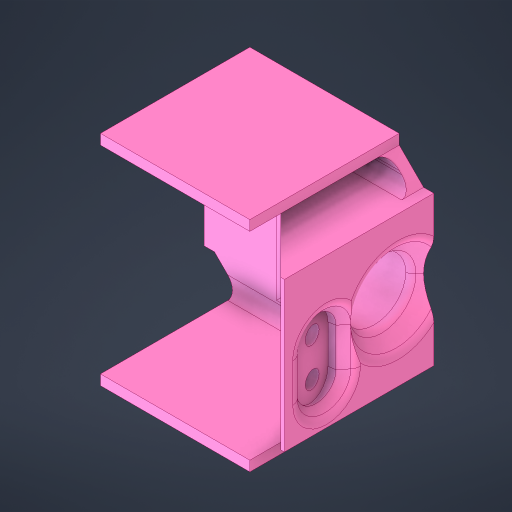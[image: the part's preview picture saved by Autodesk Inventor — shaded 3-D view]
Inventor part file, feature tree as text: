
AUTODESK INVENTOR PART (.ipt)
format: ipt  version: 2023.4 (Build 274418000, 418)  size: 642,560 bytes
history: native  units: mm
features: projected_geometry x15, extrude x14, chamfer x2, other x2, plane x1, fillet x1, reference x1
ambient origin geometry x8: Origin, YZ Plane, XZ Plane, XY Plane, X Axis, Y Axis, Z Axis, Center Point
bodies: Solid1 (feature_tree)
feature tree (36):
  plane  "Work Plane1"
  extrude  "Extrusion1"  Depth=2.5mm TaperAngle=0.0deg
  extrude  "Extrusion2"  Depth=0.075mm
  extrude  "Extrusion3"  TaperAngle=135.0deg  [1 undecoded]
  extrude  "Extrusion4"  Depth=33.95mm TaperAngle=0.0deg
  extrude  "Extrusion5"  Depth=2.5mm
  extrude  "Extrusion6"  Depth=2.5mm
  extrude  "Extrusion7"  Depth=2.5mm
  extrude  "Extrusion10"  Depth=33.95mm TaperAngle=0.0deg
  extrude  "Extrusion11"  Depth=20.0mm
  extrude  "Extrusion12"  Depth=17.5mm
  extrude  "Extrusion13"  Depth=3.875mm
  extrude  "Extrusion14"  Depth=2.5mm
  chamfer  "Chamfer1"  Distance=50.0mm
  chamfer  "Chamfer3"  Distance=4.25mm
  extrude  "Extrusion15"  Depth=3.875mm
  extrude  "Extrusion16"  Depth=5.0mm
  fillet  "Fillet1"  Radius=100.0mm
  reference  "Reference6"
  projected_geometry  "Projected Loop1"
  projected_geometry  "Projected Loop3"
  projected_geometry  "Projected Loop4"
  projected_geometry  "Projected Loop6"
  projected_geometry  "Projected Loop7"
  projected_geometry  "Projected Loop9"
  projected_geometry  "Projected Loop12"
  projected_geometry  "Projected Loop13"
  projected_geometry  "Projected Loop14"
  projected_geometry  "Projected Loop15"
  projected_geometry  "Projected Loop17"
  projected_geometry  "Projected Loop18"
  projected_geometry  "Projected Loop19"
  projected_geometry  "Projected Loop20"
  projected_geometry  "Projected Loop21"
  other  "Cube 1x1 V5.iam"
  other  "Cube 1x1 Bottom V5:1"
note: 1 required parameter value undecoded (feature->parameter linkage not recoverable at this tier; creation-order binding heuristic only, values carry confidence <= 0.55)
